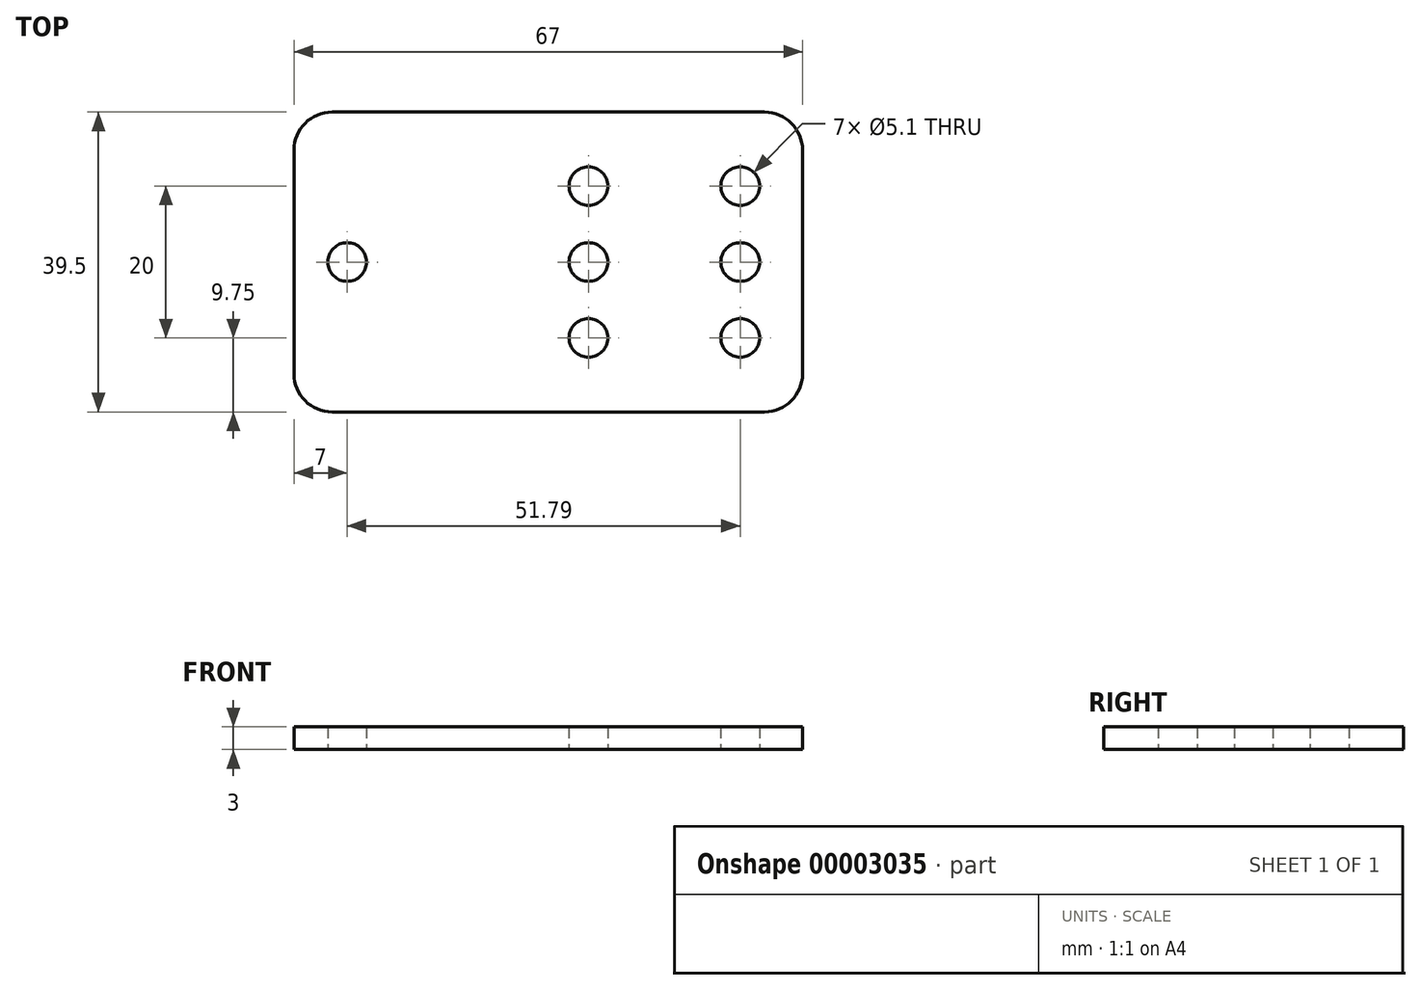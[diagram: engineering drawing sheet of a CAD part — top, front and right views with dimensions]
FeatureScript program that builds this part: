
annotation { "Feature Type Name" : "Feature", "Feature Type Description" : "" }
export const myFeature = defineFeature(function(context is Context, id is Id, definition is map)
    precondition{}
    {
        {
            var Q0;
            Q0=qCreatedBy(makeId("Top.planeOp"),FACE);
            var sketch = newSketch(context, id + "F0", { "sketchPlane" : qUnion([Q0])});
            skLineSegment(sketch, "E0.bottom", {"start": v(5, 0) * mm, "end": v(62, 0) * mm});
            skLineSegment(sketch, "E0.top", {"start": v(5, 39.5) * mm, "end": v(62, 39.5) * mm});
            skLineSegment(sketch, "E0.left", {"start": v(0, 5) * mm, "end": v(0, 34.5) * mm});
            skLineSegment(sketch, "E0.right", {"start": v(67, 5) * mm, "end": v(67, 34.5) * mm});
            skPoint(sketch, "E1.visualSharp", {"position": v(0, 39.5) * mm});
            skArc(sketch, "E1.filletArc", {"start": v(5, 39.5) * mm, "mid": v(1.46, 38.04) * mm, "end": v(0, 34.5) * mm});
            skPoint(sketch, "E2.visualSharp", {"position": v(0, 0) * mm});
            skArc(sketch, "E2.filletArc", {"start": v(0, 5) * mm, "mid": v(1.46, 1.46) * mm, "end": v(5, 0) * mm});
            skPoint(sketch, "E3.visualSharp", {"position": v(67, 0) * mm});
            skArc(sketch, "E3.filletArc", {"start": v(62, 0) * mm, "mid": v(65.54, 1.46) * mm, "end": v(67, 5) * mm});
            skPoint(sketch, "E4.visualSharp", {"position": v(67, 39.5) * mm});
            skArc(sketch, "E4.filletArc", {"start": v(67, 34.5) * mm, "mid": v(65.54, 38.04) * mm, "end": v(62, 39.5) * mm});
            skCircle(sketch, "E5", {"center": v(7, 19.75) * mm, "radius": 2.55 * mm});
            skCircle(sketch, "E6", {"center": v(38.8, 29.75) * mm, "radius": 2.55 * mm});
            skCircle(sketch, "E7", {"center": v(38.8, 19.75) * mm, "radius": 2.55 * mm});
            skCircle(sketch, "E8", {"center": v(38.8, 9.75) * mm, "radius": 2.55 * mm});
            skCircle(sketch, "E9", {"center": v(58.8, 29.75) * mm, "radius": 2.55 * mm});
            skCircle(sketch, "E10", {"center": v(58.8, 19.75) * mm, "radius": 2.55 * mm});
            skCircle(sketch, "E11", {"center": v(58.8, 9.75) * mm, "radius": 2.55 * mm});
            skSolve(sketch);
        }
        {
            var Q0;
            Q0=makeQuery(id+"F0.imprint","IMPRINT",FACE,{"disambiguationData":[TD([[makeQuery(id+"F0.imprint","IMPRINT",EDGE,{"derivedFrom":sQuery(id+"F0.wireOp",EDGE,"E0.bottom")}),1.0]])]});
            extrude(context, id + "F1", {"entities" : qUnion([Q0]), "depth" : 3 * mm});
        }
    });
